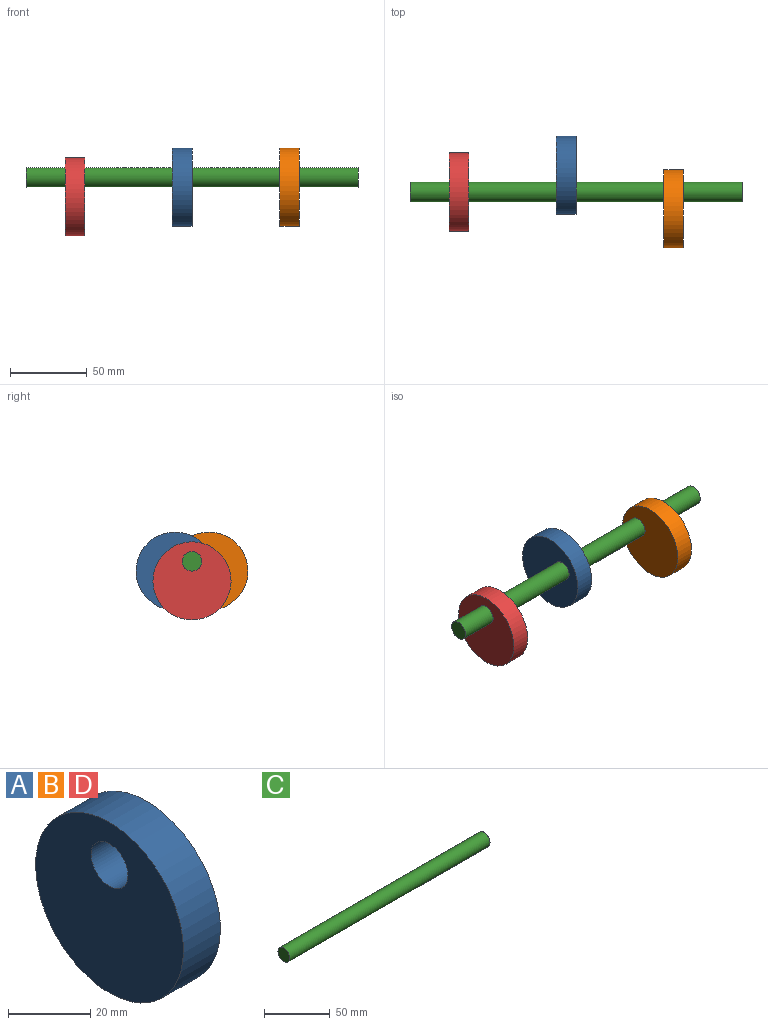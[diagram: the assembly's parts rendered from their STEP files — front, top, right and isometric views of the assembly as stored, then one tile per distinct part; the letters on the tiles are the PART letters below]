
ASSEMBLY  parts=4 mates=3
PART A: 4 faces, bbox 12.7x50.8x50.8 mm
  f0: plane 50.8x50.8mm, normal (1,0,0), area 1900.2mm2, adj f2,f3
  f1: plane 50.8x50.8mm, normal (-1,0,0), area 1900.2mm2, adj f2,f3
  f2: cylinder r=25.4mm len=50.8mm, axis (-1,0,0), area 2026.8mm2, adj f0,f1
  f3: cylinder r=6.35mm len=12.7mm, axis (-1,0,0), area 506.7mm2, adj f0,f1
PART B: same geometry as A
PART C: 3 faces, bbox 215.9x12.7x12.7 mm
  f0: plane 12.7x12.7mm, normal (-1,0,0), area 126.7mm2, adj f2
  f1: plane 12.7x12.7mm, normal (1,0,0), area 126.7mm2, adj f2
  f2: cylinder r=6.35mm len=215.9mm, axis (-1,0,0), area 8614mm2, adj f0,f1
PART D: same geometry as A
PLACE A rot(axis=(1,0,0),60deg) t=(63.5,49.49,-28.57)mm
PLACE B rot(axis=(-1,0,0),60deg) t=(133.35,-49.49,-28.58)mm
PLACE C rot(axis=(1,0,0),180deg) t=(-6.35,0,57.15)mm
PLACE D t=(-6.35,0,-57.15)mm
MATE fastened C.f2 <-> A.f3  axis (-1,0,0) through (-6.35,0,0)mm
MATE fastened C.f2 <-> B.f3  axis (-1,0,0) through (63.5,0,0)mm
MATE fastened C.f2 <-> D.f3  axis (-1,0,0) through (-76.2,0,0)mm
